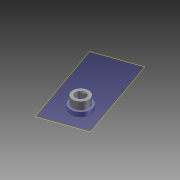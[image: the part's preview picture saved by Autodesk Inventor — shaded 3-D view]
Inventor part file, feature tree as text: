
AUTODESK INVENTOR PART (.ipt)
format: ipt  version: 2012 (Build 160160000, 160)  size: 118,784 bytes
history: native  units: mm
features: extrude x7, sketch x7, projected_geometry x2, plane x1, reference x1
ambient origin geometry x8: Origin, YZ Plane, XZ Plane, XY Plane, X Axis, Y Axis, Z Axis, Center Point
bodies: Solid1 (feature_tree)
feature tree (18):
  plane  "Work Plane1"
  extrude  "Extrusion4"  Depth=3.0mm TaperAngle=0.0deg
  extrude  "Extrusion5"  Depth=13.2mm
  extrude  "Extrusion10"  Depth=3.762mm
  extrude  "Extrusion11"  Depth=0.3mm TaperAngle=0.0deg
  extrude  "Extrusion12"  Depth=5.0mm TaperAngle=0.0deg
  extrude  "Extrusion13"  Depth=0.5mm TaperAngle=0.0deg
  extrude  "Extrusion14"  [1 undecoded]
  sketch  "Sketch5"  dims[d13=1.0mm d14=3.0mm d15=0.0mm]
  reference  "Reference1"
  sketch  "Sketch6"  dims[d16=0.3mm d17=0.0mm d26=13.2mm]
  sketch  "Sketch11"  dims[d27=6.6mm d28=3.762mm]
  sketch  "Sketch12"  dims[d29=2.7mm d30=0.0mm d31=0.3mm d32=0.0mm]
  projected_geometry  "Projected Loop4"
  sketch  "Sketch13"  dims[d33=10.6mm d34=5.0mm d35=0.0mm]
  sketch  "Sketch14"  dims[d36=5.0mm d37=0.0mm d38=0.5mm d39=0.0mm]
  projected_geometry  "Projected Loop5"
  sketch  "Sketch15"
note: 1 required parameter value undecoded (feature->parameter linkage not recoverable at this tier; creation-order binding heuristic only, values carry confidence <= 0.55)
